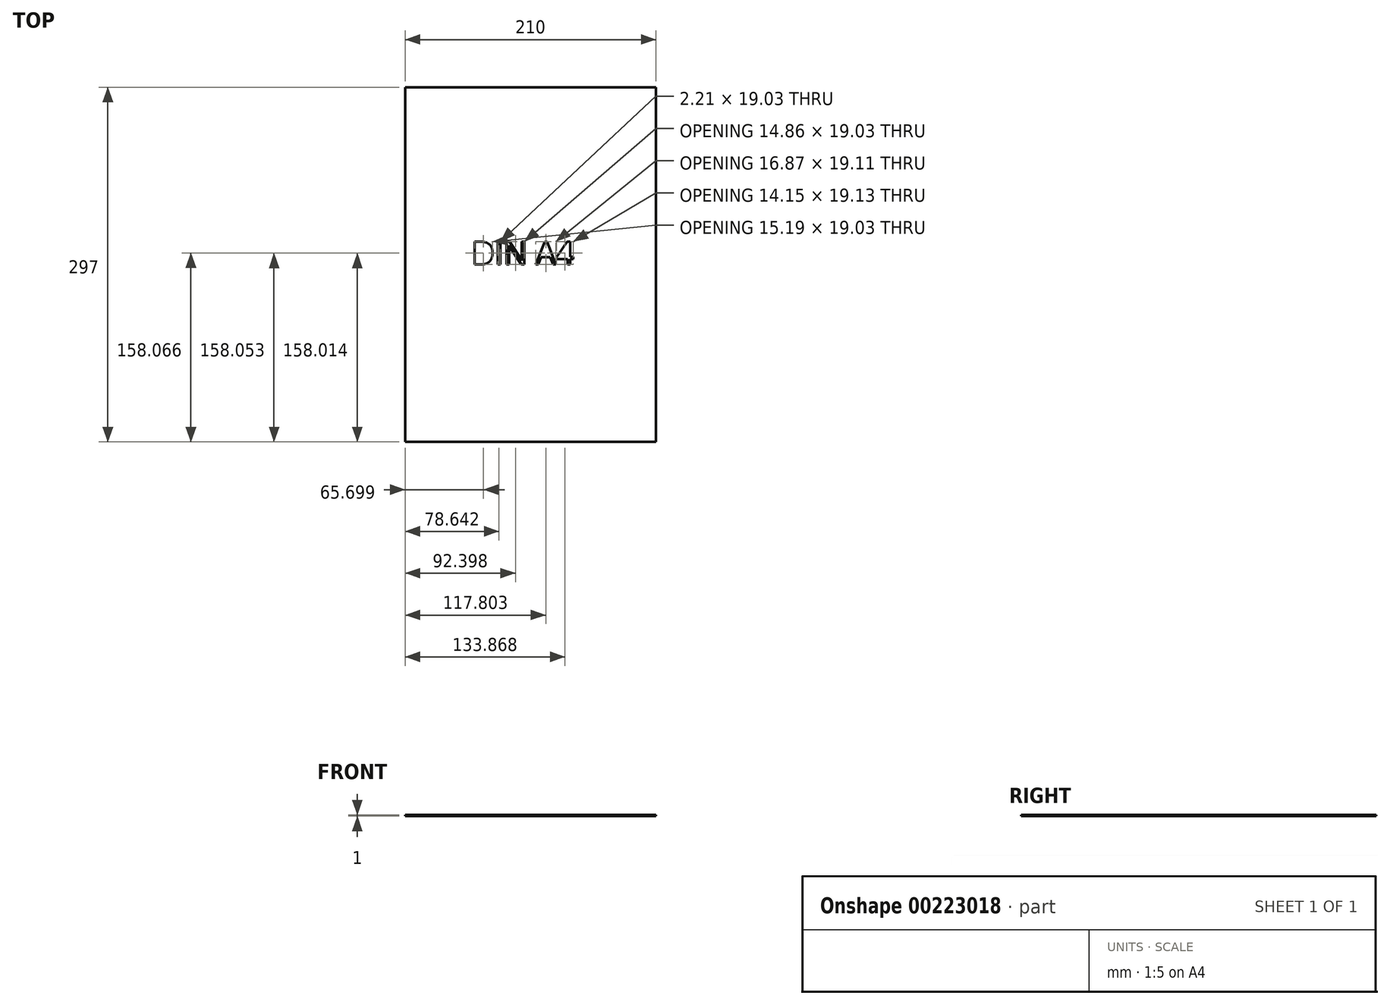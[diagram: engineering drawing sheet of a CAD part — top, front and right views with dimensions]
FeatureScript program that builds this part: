
annotation { "Feature Type Name" : "Feature", "Feature Type Description" : "" }
export const myFeature = defineFeature(function(context is Context, id is Id, definition is map)
    precondition{}
    {
        {
            var Q0;
            Q0=qCreatedBy(makeId("Top.planeOp"),FACE);
            var sketch = newSketch(context, id + "F0", { "sketchPlane" : qUnion([Q0])});
            skLineSegment(sketch, "E0.bottom", {"start": v(105, 148.5) * mm, "end": v(-105, 148.5) * mm});
            skLineSegment(sketch, "E0.top", {"start": v(105, -148.5) * mm, "end": v(-105, -148.5) * mm});
            skLineSegment(sketch, "E0.left", {"start": v(105, 148.5) * mm, "end": v(105, -148.5) * mm});
            skLineSegment(sketch, "E0.right", {"start": v(-105, 148.5) * mm, "end": v(-105, -148.5) * mm});
            skPoint(sketch, "E0.middle", {"position": v(0, 0) * mm});
            skText(sketch, "E1", { "text": "DIN A4", "fontName": "OpenSans-Regular.ttf"});
            const initialGuessF0  = {"E1": [-0.04951, 0, 1, 0, 0.01919]};
            skSetInitialGuess(sketch, initialGuessF0);
            skSolve(sketch);
        }
        {
            var Q0;
            Q0 = qSketchRegion(id + "F0", true);
            extrude(context, id + "F1", {"entities" : qUnion([Q0]), "depth" : 1 * mm});
        }
    });
